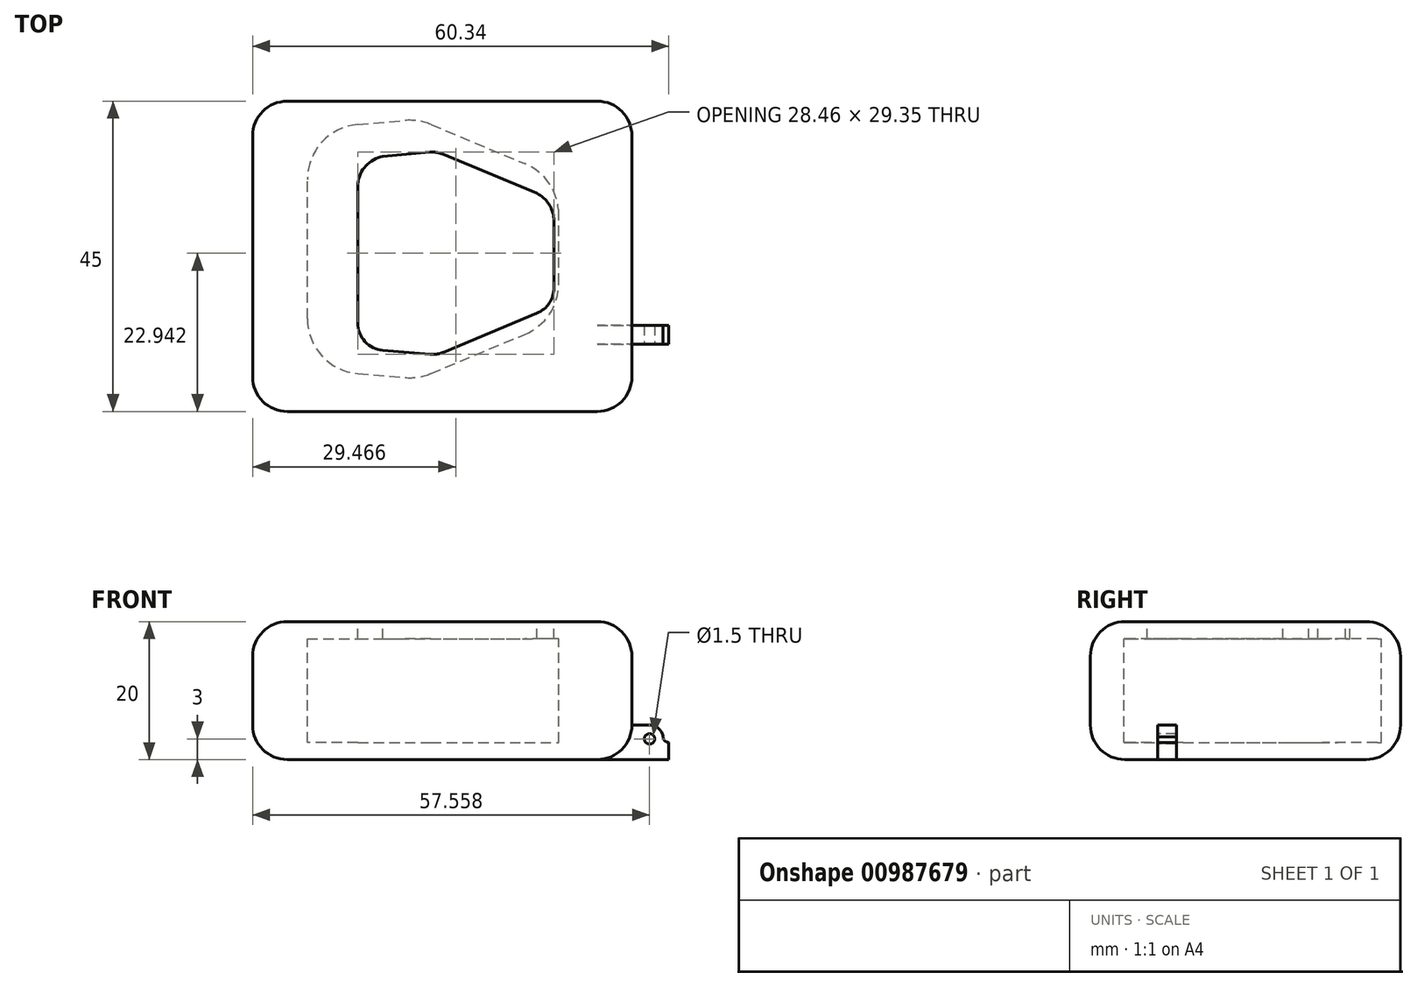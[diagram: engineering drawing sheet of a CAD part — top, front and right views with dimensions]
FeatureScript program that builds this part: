
annotation { "Feature Type Name" : "Feature", "Feature Type Description" : "" }
export const myFeature = defineFeature(function(context is Context, id is Id, definition is map)
    precondition{}
    {
        {
            var Q0;
            Q0=qCreatedBy(makeId("Top.planeOp"),FACE);
            var sketch = newSketch(context, id + "F0", { "sketchPlane" : qUnion([Q0])});
            skLineSegment(sketch, "E0.bottom", {"start": v(27.5, -22.5) * mm, "end": v(-27.5, -22.5) * mm});
            skLineSegment(sketch, "E0.top", {"start": v(27.5, 22.5) * mm, "end": v(-27.5, 22.5) * mm});
            skLineSegment(sketch, "E0.left", {"start": v(27.5, -22.5) * mm, "end": v(27.5, 22.5) * mm});
            skLineSegment(sketch, "E0.right", {"start": v(-27.5, -22.5) * mm, "end": v(-27.5, 22.5) * mm});
            skPoint(sketch, "E0.middle", {"position": v(0, 0) * mm});
            skSolve(sketch);
        }
        {
            var Q0;
            Q0 = qSketchRegion(id + "F0", true);
            extrude(context, id + "F1", {"entities" : qUnion([Q0]), "depth" : 20 * mm, "offsetDistance" : 25 * mm});
        }
        {
            var Q0;
            Q0=makeQuery(id+"F1.opExtrude","SWEPT_FACE",FACE,{"disambiguationData":[OSD([sQuery(id+"F0.wireOp",EDGE,"E0.bottom")])]});
            var sketch = newSketch(context, id + "F2", { "sketchPlane" : qUnion([Q0])});
            skLineSegment(sketch, "E1", {"start": v(0, 0) * mm, "end": v(-10, 0) * mm, "construction": true});
            skLineSegment(sketch, "E2", {"start": v(0, 0) * mm, "end": v(10, 0) * mm, "construction": true});
            skSolve(sketch);
        }
        {
            var Q0;
            Q0=qCreatedBy(makeId("Right.planeOp"),FACE);
            var Q1;
            Q1=sQuery(id+"F2.wireOp",VERTEX,"E1.end");
            cPlane(context, id + "F3", {"entities" : qUnion([Q0, Q1]), "cplaneType" : CPlaneType.PLANE_POINT, "offset" : 25 * mm, "width" : 150 * mm, "height" : 150 * mm});
        }
        {
            var Q0;
            Q0=makeQuery(id+"F1.opExtrude","CAP_FACE",FACE,{"disambiguationData":[OSD([sQuery(id+"F0.wireOp",EDGE,"E0.bottom"),sQuery(id+"F0.wireOp",EDGE,"E0.top"),sQuery(id+"F0.wireOp",EDGE,"E0.left"),sQuery(id+"F0.wireOp",EDGE,"E0.right")])],"isStart":false});
            var sketch = newSketch(context, id + "F4", { "sketchPlane" : qUnion([Q0])});
            skLineSegment(sketch, "E3", {"start": v(-19.57, 1.06) * mm, "end": v(-19.57, -9.03) * mm});
            skLineSegment(sketch, "E4", {"start": v(-12.25, -17) * mm, "end": v(-5.42, -17.59) * mm});
            skLineSegment(sketch, "E5", {"start": v(-1.66, -17) * mm, "end": v(11.97, -11.33) * mm});
            skLineSegment(sketch, "E6", {"start": v(16.9, -3.95) * mm, "end": v(16.9, 1.06) * mm});
            skPoint(sketch, "E7.visualSharp", {"position": v(-19.57, -16.38) * mm});
            skArc(sketch, "E7.filletArc", {"start": v(-19.57, -9.03) * mm, "mid": v(-17.46, -14.44) * mm, "end": v(-12.25, -17) * mm});
            skPoint(sketch, "E8.visualSharp", {"position": v(16.9, -9.28) * mm});
            skArc(sketch, "E8.filletArc", {"start": v(11.97, -11.33) * mm, "mid": v(15.55, -8.39) * mm, "end": v(16.9, -3.95) * mm});
            skLineSegment(sketch, "E9.MirrorCS", {"start": v(-19.57, 1.06) * mm, "end": v(-19.57, 11.15) * mm});
            skArc(sketch, "E10.MirrorCS", {"start": v(-19.57, 11.15) * mm, "mid": v(-17.46, 16.56) * mm, "end": v(-12.25, 19.12) * mm});
            skLineSegment(sketch, "E11.MirrorCS", {"start": v(-12.25, 19.12) * mm, "end": v(-5.42, 19.7) * mm});
            skLineSegment(sketch, "E12.MirrorCS", {"start": v(-12.25, 19.12) * mm, "end": v(-3.47, 19.87) * mm});
            skLineSegment(sketch, "E13.MirrorCS", {"start": v(-1.66, 19.12) * mm, "end": v(11.97, 13.45) * mm});
            skArc(sketch, "E14.MirrorCS", {"start": v(11.97, 13.45) * mm, "mid": v(15.55, 10.5) * mm, "end": v(16.9, 6.07) * mm});
            skLineSegment(sketch, "E15.MirrorCS", {"start": v(16.9, 6.07) * mm, "end": v(16.9, 1.06) * mm});
            skPoint(sketch, "E16.visualSharp", {"position": v(-3.47, -17.75) * mm});
            skArc(sketch, "E16.filletArc", {"start": v(-5.42, -17.59) * mm, "mid": v(-3.5, -17.52) * mm, "end": v(-1.66, -17) * mm});
            skPoint(sketch, "E17.visualSharp", {"position": v(-3.47, 19.87) * mm});
            skArc(sketch, "E17.filletArc", {"start": v(-1.66, 19.12) * mm, "mid": v(-3.5, 19.64) * mm, "end": v(-5.42, 19.7) * mm});
            skSolve(sketch);
        }
        {
            var Q0;
            Q0=makeQuery(id+"F4.imprint","IMPRINT",FACE,{"disambiguationData":[TD([[makeQuery(id+"F4.imprint","IMPRINT",EDGE,{"derivedFrom":sQuery(id+"F4.wireOp",EDGE,"E3")}),1.0]])]});
            extrude(context, id + "F5", {"entities" : qUnion([Q0]), "operationType" : NewBodyOperationType.REMOVE, "oppositeDirection" : true, "depth" : 17.5 * mm, "offsetDistance" : 25 * mm});
        }
        {
            var Q0;
            Q0=makeQuery(id+"F1.opExtrude","CAP_FACE",FACE,{"disambiguationData":[OSD([sQuery(id+"F0.wireOp",EDGE,"E0.bottom"),sQuery(id+"F0.wireOp",EDGE,"E0.top"),sQuery(id+"F0.wireOp",EDGE,"E0.left"),sQuery(id+"F0.wireOp",EDGE,"E0.right")])],"isStart":false});
            var sketch = newSketch(context, id + "F6", { "sketchPlane" : qUnion([Q0])});
            skLineSegment(sketch, "E18", {"start": v(-16.26, 0.44) * mm, "end": v(-16.26, -9.65) * mm});
            skLineSegment(sketch, "E19", {"start": v(-8.95, -17.62) * mm, "end": v(-2.11, -18.2) * mm});
            skLineSegment(sketch, "E20", {"start": v(1.64, -17.62) * mm, "end": v(15.27, -11.95) * mm});
            skLineSegment(sketch, "E21", {"start": v(20.2, -4.56) * mm, "end": v(20.2, 0.44) * mm});
            skPoint(sketch, "E22.visualSharp", {"position": v(-16.26, -17) * mm});
            skArc(sketch, "E22.filletArc", {"start": v(-16.26, -9.65) * mm, "mid": v(-14.16, -15.06) * mm, "end": v(-8.95, -17.62) * mm});
            skPoint(sketch, "E23.visualSharp", {"position": v(20.2, -9.9) * mm});
            skArc(sketch, "E23.filletArc", {"start": v(15.27, -11.95) * mm, "mid": v(18.85, -9) * mm, "end": v(20.2, -4.56) * mm});
            skLineSegment(sketch, "E24.MirrorCS", {"start": v(-16.26, 0.44) * mm, "end": v(-16.26, 10.53) * mm});
            skArc(sketch, "E25.MirrorCS", {"start": v(-16.3, 10.01) * mm, "mid": v(-14.03, 15.83) * mm, "end": v(-8.43, 18.58) * mm});
            skLineSegment(sketch, "E26.MirrorCS", {"start": v(-8.95, 18.5) * mm, "end": v(-2.11, 19.09) * mm});
            skLineSegment(sketch, "E27.MirrorCS", {"start": v(1.64, 18.5) * mm, "end": v(15.27, 12.83) * mm});
            skArc(sketch, "E28.MirrorCS", {"start": v(14.92, 13) * mm, "mid": v(18.77, 9.83) * mm, "end": v(20.21, 5.06) * mm});
            skLineSegment(sketch, "E29.MirrorCS", {"start": v(20.2, 5.45) * mm, "end": v(20.2, 0.44) * mm});
            skPoint(sketch, "E30.visualSharp", {"position": v(-0.16, -18.37) * mm});
            skArc(sketch, "E30.filletArc", {"start": v(-2.11, -18.2) * mm, "mid": v(-0.2, -18.14) * mm, "end": v(1.64, -17.62) * mm});
            skPoint(sketch, "E31.visualSharp", {"position": v(-0.16, 19.25) * mm});
            skArc(sketch, "E31.filletArc", {"start": v(1.64, 18.5) * mm, "mid": v(-0.2, 19.02) * mm, "end": v(-2.11, 19.09) * mm});
            skLineSegment(sketch, "E32.0", {"start": v(-12.26, 0.44) * mm, "end": v(-12.26, -9.65) * mm});
            skLineSegment(sketch, "E32.1", {"start": v(-12.26, 0.44) * mm, "end": v(-12.26, 10.53) * mm});
            skArc(sketch, "E32.2", {"start": v(-12.26, 10.53) * mm, "mid": v(-11.08, 13.12) * mm, "end": v(-8.6, 14.52) * mm});
            skArc(sketch, "E32.3", {"start": v(13.73, -8.26) * mm, "mid": v(15.52, -6.78) * mm, "end": v(16.2, -4.56) * mm});
            skLineSegment(sketch, "E32.4", {"start": v(0.1, -13.93) * mm, "end": v(13.73, -8.26) * mm});
            skArc(sketch, "E32.5", {"start": v(-1.77, -14.22) * mm, "mid": v(-0.82, -14.19) * mm, "end": v(0.1, -13.93) * mm});
            skLineSegment(sketch, "E32.6", {"start": v(-8.6, -13.64) * mm, "end": v(-1.77, -14.22) * mm});
            skLineSegment(sketch, "E32.7", {"start": v(16.2, -4.56) * mm, "end": v(16.2, 0.44) * mm});
            skLineSegment(sketch, "E32.8", {"start": v(16.2, 5.45) * mm, "end": v(16.2, 0.44) * mm});
            skArc(sketch, "E32.9", {"start": v(13.73, 9.14) * mm, "mid": v(15.44, 7.61) * mm, "end": v(16.2, 5.45) * mm});
            skArc(sketch, "E32.10", {"start": v(-12.26, -9.65) * mm, "mid": v(-11.21, -12.36) * mm, "end": v(-8.6, -13.64) * mm});
            skLineSegment(sketch, "E32.11", {"start": v(0.1, 14.81) * mm, "end": v(13.73, 9.14) * mm});
            skArc(sketch, "E32.12", {"start": v(0.1, 14.81) * mm, "mid": v(-0.82, 15.07) * mm, "end": v(-1.77, 15.1) * mm});
            skLineSegment(sketch, "E32.13", {"start": v(-8.6, 14.52) * mm, "end": v(-1.77, 15.1) * mm});
            skLineSegment(sketch, "E33.0", {"start": v(-4.22, -5.87) * mm, "end": v(-2.02, -6.06) * mm});
            skLineSegment(sketch, "E33.1", {"start": v(8.24, -1.8) * mm, "end": v(8.24, 2.88) * mm});
            skLineSegment(sketch, "E33.2", {"start": v(8.24, 2.88) * mm, "end": v(-2.02, 7.15) * mm});
            skLineSegment(sketch, "E33.3", {"start": v(-2.02, -6.06) * mm, "end": v(8.24, -1.8) * mm});
            skLineSegment(sketch, "E33.4", {"start": v(-2.02, 7.15) * mm, "end": v(-4.22, 6.96) * mm});
            skLineSegment(sketch, "E33.5", {"start": v(-4.22, 6.96) * mm, "end": v(-4.22, -5.87) * mm});
            skSolve(sketch);
        }
        {
            var Q0;
            Q0=makeQuery(id+"F6.imprint","IMPRINT",FACE,{"disambiguationData":[TD([[makeQuery(id+"F6.imprint","IMPRINT",EDGE,{"derivedFrom":sQuery(id+"F6.wireOp",EDGE,"E32.0")}),-1.0]])]});
            extrude(context, id + "F7", {"entities" : qUnion([Q0]), "operationType" : NewBodyOperationType.ADD, "oppositeDirection" : true, "depth" : 2.5 * mm, "offsetDistance" : 25 * mm});
        }
        {
            var Q0;
            Q0=makeQuery(id+"F1.opExtrude","SWEPT_FACE",FACE,{"disambiguationData":[OSD([sQuery(id+"F0.wireOp",EDGE,"E0.left")])]});
            var sketch = newSketch(context, id + "F8", { "sketchPlane" : qUnion([Q0])});
            skSolve(sketch);
        }
        {
            var Q0;
            Q0=makeQuery(id+"F1.opExtrude","SWEPT_EDGE",EDGE,{"disambiguationData":[OSD([sQuery(id+"F0.wireOp",EDGE,"E0.bottom"),sQuery(id+"F0.wireOp",EDGE,"E0.right")])]});
            var Q1;
            Q1=makeQuery(id+"F1.opExtrude","CAP_EDGE",EDGE,{"disambiguationData":[OSD([sQuery(id+"F0.wireOp",EDGE,"E0.bottom")])],"isStart":false});
            fillet(context, id + "F9", {"entities" : qUnion([Q0, Q1]), "radius" : 5 * mm, "tangentPropagation" : true, "allowEdgeOverflow" : false});
        }
        {
            var Q0;
            Q0=makeQuery(id+"F1.opExtrude","SWEPT_EDGE",EDGE,{"disambiguationData":[OSD([sQuery(id+"F0.wireOp",EDGE,"E0.top"),sQuery(id+"F0.wireOp",EDGE,"E0.right")])]});
            var Q1;
            {var subQ1=sQuery(id+"F0.wireOp",EDGE,"E0.right");var subQ2=sQuery(id+"F0.wireOp",EDGE,"E0.top");Q1=makeQuery(id+"FJ7BhoPzGbSxfPN_1.boolean.opBoolean","SPLIT",EDGE,{"disambiguationData":[TD([makeQuery(id+"F1.opExtrude","SWEPT_FACE",FACE,{"disambiguationData":[OSD([subQ1])]})])],"derivedFrom":makeQuery(id+"F1.opExtrude","CAP_EDGE",EDGE,{"disambiguationData":[OSD([subQ2])],"isStart":true})});}
            fillet(context, id + "F10", {"entities" : qUnion([Q0, Q1]), "radius" : 5 * mm, "tangentPropagation" : true, "allowEdgeOverflow" : false});
        }
        {
            var Q0;
            {var subQ0=sQuery(id+"F0.wireOp",EDGE,"E0.right");Q0=makeQuery(id+"F10.opFillet","BLEND_EDGE",EDGE,{"blendedFrom":[makeQuery(id+"F1.opExtrude","SWEPT_EDGE",EDGE,{"disambiguationData":[OSD([sQuery(id+"F0.wireOp",EDGE,"E0.top"),subQ0])]}),makeQuery(id+"F1.opExtrude","SWEPT_FACE",FACE,{"disambiguationData":[OSD([subQ0])]})],"blendedInto":[makeQuery(id+"F1.opExtrude","SWEPT_FACE",FACE,{"disambiguationData":[OSD([subQ0])]})]});}
            var Q1;
            Q1=makeQuery(id+"F1.opExtrude","CAP_EDGE",EDGE,{"disambiguationData":[OSD([sQuery(id+"F0.wireOp",EDGE,"E0.right")])],"isStart":false});
            fillet(context, id + "F11", {"entities" : qUnion([Q0, Q1]), "radius" : 5 * mm, "tangentPropagation" : true, "allowEdgeOverflow" : false});
        }
        {
            var Q0;
            {var subQ0=sQuery(id+"F1VljDQsBSWXWAY_1.wireOp",EDGE,"aa749f7b-bef2-4c3b-88c6-d728afbe9ac0");var subQ1=sQuery(id+"F0.wireOp",EDGE,"E0.right");var subQ2=sQuery(id+"F0.wireOp",EDGE,"E0.bottom");var subQ3=makeQuery(id+"FR4HHGLlpoIwAa3_1.1.FJ7BhoPzGbSxfPN_1.boolean.opBoolean","MERGE",FACE,{"derivedFrom":[makeQuery(id+"FGjuvG77NJaLf5O_1.1.FJ7BhoPzGbSxfPN_1.boolean.opBoolean","MERGE",FACE,{"derivedFrom":[makeQuery(id+"FJ7BhoPzGbSxfPN_1.boolean.opBoolean","MERGE",FACE,{"derivedFrom":[makeQuery(id+"F1.opExtrude","CAP_FACE",FACE,{"disambiguationData":[OSD([subQ2,sQuery(id+"F0.wireOp",EDGE,"E0.top"),sQuery(id+"F0.wireOp",EDGE,"E0.left"),subQ1])],"isStart":true}),makeQuery(id+"FJ7BhoPzGbSxfPN_1.opExtrude","SWEPT_FACE",FACE,{"disambiguationData":[OSD([subQ0])]})]}),makeQuery(id+"FGjuvG77NJaLf5O_1.1.FJ7BhoPzGbSxfPN_1.opExtrude","SWEPT_FACE",FACE,{"disambiguationData":[OSD([subQ0])]})]}),makeQuery(id+"FR4HHGLlpoIwAa3_1.1.FJ7BhoPzGbSxfPN_1.opExtrude","SWEPT_FACE",FACE,{"disambiguationData":[OSD([subQ0])]})]});Q0=makeQuery(id+"F9.opFillet","BLEND_EDGE",EDGE,{"blendedFrom":[makeQuery(id+"F1.opExtrude","SWEPT_EDGE",EDGE,{"disambiguationData":[OSD([subQ2,subQ1])]}),makeQuery(id+"FcU7kem4Tgbkafd_1.boolean.opBoolean","MERGE",FACE,{"derivedFrom":[subQ3,makeQuery(id+"FcU7kem4Tgbkafd_1.opPattern","COPY",FACE,{"derivedFrom":subQ3,"instanceName":"1"})]})],"blendedInto":[makeQuery(id+"FcU7kem4Tgbkafd_1.boolean.opBoolean","MERGE",FACE,{"derivedFrom":[subQ3,makeQuery(id+"FcU7kem4Tgbkafd_1.opPattern","COPY",FACE,{"derivedFrom":subQ3,"instanceName":"1"})]})]});}
            var Q1;
            {var subQ0=sQuery(id+"F0.wireOp",EDGE,"E0.bottom");Q1=makeQuery(id+"F9.opFillet","BLEND_EDGE",EDGE,{"blendedFrom":[makeQuery(id+"F1.opExtrude","SWEPT_EDGE",EDGE,{"disambiguationData":[OSD([subQ0,sQuery(id+"F0.wireOp",EDGE,"E0.right")])]}),makeQuery(id+"F1.opExtrude","SWEPT_FACE",FACE,{"disambiguationData":[OSD([subQ0])]})],"blendedInto":[makeQuery(id+"F1.opExtrude","SWEPT_FACE",FACE,{"disambiguationData":[OSD([subQ0])]})]});}
            fillet(context, id + "F12", {"entities" : qUnion([Q0, Q1]), "radius" : 5 * mm, "tangentPropagation" : true, "allowEdgeOverflow" : false});
        }
        {
            var Q0;
            Q0=makeQuery(id+"F1.opExtrude","SWEPT_EDGE",EDGE,{"disambiguationData":[OSD([sQuery(id+"F0.wireOp",EDGE,"E0.top"),sQuery(id+"F0.wireOp",EDGE,"E0.left")])]});
            var Q1;
            {var subQ0=sQuery(id+"F0.wireOp",EDGE,"E0.top");Q1=makeQuery(id+"F11.opFillet","BLEND_EDGE",EDGE,{"disambiguationData":[OD(1.0)],"blendedFrom":[makeQuery(id+"F1.opExtrude","CAP_EDGE",EDGE,{"disambiguationData":[OSD([subQ0])],"isStart":false}),makeQuery(id+"F1.opExtrude","CAP_FACE",FACE,{"disambiguationData":[OSD([sQuery(id+"F0.wireOp",EDGE,"E0.bottom"),subQ0,sQuery(id+"F0.wireOp",EDGE,"E0.left"),sQuery(id+"F0.wireOp",EDGE,"E0.right")])],"isStart":false})],"blendedInto":[makeQuery(id+"F1.opExtrude","CAP_FACE",FACE,{"disambiguationData":[OSD([sQuery(id+"F0.wireOp",EDGE,"E0.bottom"),subQ0,sQuery(id+"F0.wireOp",EDGE,"E0.left"),sQuery(id+"F0.wireOp",EDGE,"E0.right")])],"isStart":false})]});}
            fillet(context, id + "F13", {"entities" : qUnion([Q0, Q1]), "radius" : 5 * mm, "tangentPropagation" : true, "allowEdgeOverflow" : false});
        }
        {
            var Q0;
            {var subQ0=sQuery(id+"F0.wireOp",EDGE,"E0.bottom");Q0=makeQuery(id+"F2.imprint","IMPRINT",FACE,{"disambiguationData":[TD([[makeQuery(id+"F2.imprint","IMPRINT",EDGE,{"derivedFrom":makeQuery(id+"F1.opExtrude","CAP_EDGE",EDGE,{"disambiguationData":[OSD([subQ0])],"isStart":true})}),-1.0]])]});}
            cPlane(context, id + "F14", {"entities" : qUnion([Q0]), "cplaneType" : CPlaneType.OFFSET, "offset" : 9.75 * mm, "oppositeDirection" : true, "width" : 150 * mm, "height" : 150 * mm});
        }
        {
            var Q0;
            Q0=qCreatedBy(id+"F14.planeOp",FACE);
            var sketch = newSketch(context, id + "F15", { "sketchPlane" : qUnion([Q0])});
            skLineSegment(sketch, "E34.MirrorCS", {"start": v(27.5, 5) * mm, "end": v(30.06, 5) * mm});
            skArc(sketch, "E35.MirrorCS", {"start": v(30.06, 5) * mm, "mid": v(31.36, 4.52) * mm, "end": v(32.04, 3.3) * mm});
            skArc(sketch, "E36.MirrorCS", {"start": v(32.84, 2.5) * mm, "mid": v(32.27, 2.73) * mm, "end": v(32.04, 3.3) * mm});
            skLineSegment(sketch, "E37", {"start": v(32.84, 0) * mm, "end": v(32.84, 2.5) * mm});
            skCircle(sketch, "E38", {"center": v(30.06, 3) * mm, "radius": 0.75 * mm});
            skLineSegment(sketch, "E39", {"start": v(27.5, 5) * mm, "end": v(27.5, 5) * mm});
            skLineSegment(sketch, "E40", {"start": v(22.5, 0) * mm, "end": v(22.5, 0) * mm});
            skPoint(sketch, "E41.visualSharp", {"position": v(27.5, 0) * mm});
            skArc(sketch, "E41.filletArc", {"start": v(22.5, 0) * mm, "mid": v(26.04, 1.46) * mm, "end": v(27.5, 5) * mm});
            skLineSegment(sketch, "E42", {"start": v(32.84, 0) * mm, "end": v(22.5, 0) * mm});
            skSolve(sketch);
        }
        {
            var Q0;
            Q0=makeQuery(id+"F15.imprint","IMPRINT",FACE,{"disambiguationData":[TD([[makeQuery(id+"F15.imprint","IMPRINT",EDGE,{"derivedFrom":sQuery(id+"F15.wireOp",EDGE,"E34.MirrorCS")}),-1.0]])]});
            extrude(context, id + "F16", {"entities" : qUnion([Q0]), "operationType" : NewBodyOperationType.ADD, "oppositeDirection" : true, "depth" : 2.75 * mm, "offsetDistance" : 25 * mm});
        }
    });
